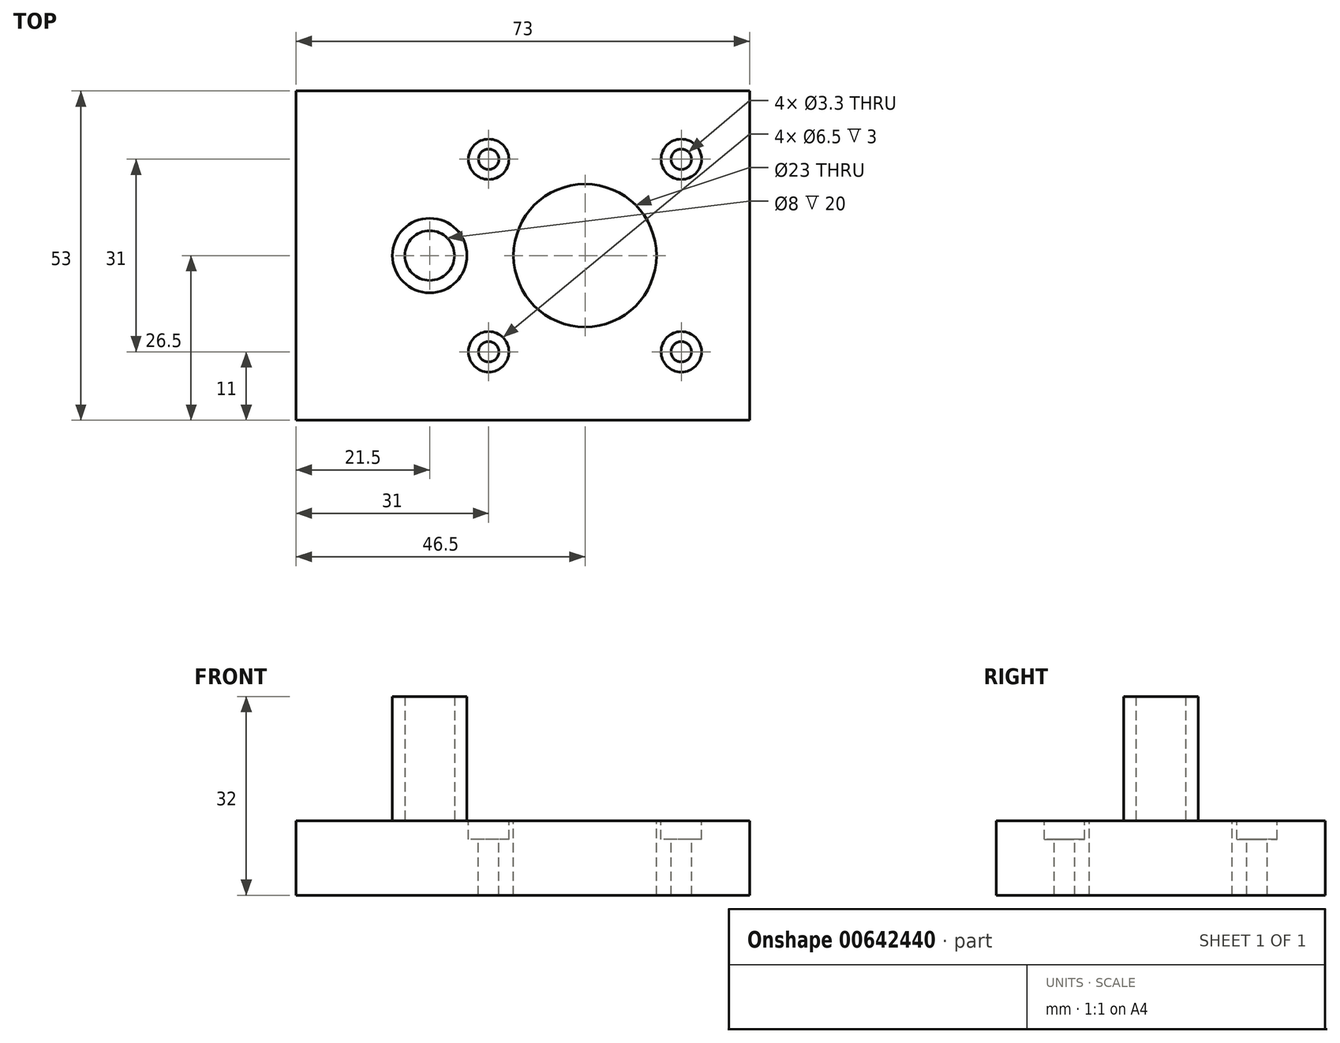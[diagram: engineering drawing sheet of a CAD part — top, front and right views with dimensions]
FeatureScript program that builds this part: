
annotation { "Feature Type Name" : "Feature", "Feature Type Description" : "" }
export const myFeature = defineFeature(function(context is Context, id is Id, definition is map)
    precondition{}
    {
        {
            var Q0;
            Q0=qCreatedBy(makeId("Top.planeOp"),FACE);
            var sketch = newSketch(context, id + "F0", { "sketchPlane" : qUnion([Q0])});
            skLineSegment(sketch, "E0.bottom", {"start": v(36.5, -26.5) * mm, "end": v(-36.5, -26.5) * mm});
            skLineSegment(sketch, "E0.top", {"start": v(36.5, 26.5) * mm, "end": v(-36.5, 26.5) * mm});
            skLineSegment(sketch, "E0.left", {"start": v(36.5, -26.5) * mm, "end": v(36.5, 26.5) * mm});
            skLineSegment(sketch, "E0.right", {"start": v(-36.5, -26.5) * mm, "end": v(-36.5, 26.5) * mm});
            skPoint(sketch, "E0.middle", {"position": v(0, 0) * mm});
            skLineSegment(sketch, "E1.bottom", {"start": v(25.5, -15.5) * mm, "end": v(-5.5, -15.5) * mm, "construction": true});
            skLineSegment(sketch, "E1.top", {"start": v(25.5, 15.5) * mm, "end": v(-5.5, 15.5) * mm, "construction": true});
            skLineSegment(sketch, "E1.left", {"start": v(25.5, -15.5) * mm, "end": v(25.5, 15.5) * mm, "construction": true});
            skLineSegment(sketch, "E1.right", {"start": v(-5.5, -15.5) * mm, "end": v(-5.5, 15.5) * mm, "construction": true});
            skPoint(sketch, "E1.middle", {"position": v(10, 0) * mm});
            skCircle(sketch, "E2", {"center": v(-15, 0) * mm, "radius": 6 * mm});
            skPoint(sketch, "E3", {"position": v(-5.5, 15.5) * mm});
            skPoint(sketch, "E4", {"position": v(25.5, 15.5) * mm});
            skPoint(sketch, "E5", {"position": v(25.5, -15.5) * mm});
            skPoint(sketch, "E6", {"position": v(-5.5, -15.5) * mm});
            skCircle(sketch, "E7", {"center": v(-15, 0) * mm, "radius": 4 * mm});
            skCircle(sketch, "E8", {"center": v(10, 0) * mm, "radius": 11.5 * mm});
            skSolve(sketch);
        }
        {
            var Q0;
            Q0 = qSketchRegion(id + "F0", true);
            var Q1;
            Q1=makeQuery(id+"F0.imprint","IMPRINT",FACE,{"disambiguationData":[TD([[makeQuery(id+"F0.imprint","IMPRINT",EDGE,{"derivedFrom":sQuery(id+"F0.wireOp",EDGE,"E2")}),1.0]])]});
            var Q2;
            Q2=makeQuery(id+"F0.imprint","IMPRINT",FACE,{"disambiguationData":[TD([[makeQuery(id+"F0.imprint","IMPRINT",EDGE,{"derivedFrom":sQuery(id+"F0.wireOp",EDGE,"E7")}),1.0]])]});
            extrude(context, id + "F1", {"entities" : qUnion([Q0, Q1, Q2]), "oppositeDirection" : true, "depth" : 12 * mm, "offsetDistance" : 25 * mm});
        }
        {
            var Q0;
            Q0=makeQuery(id+"F0.imprint","IMPRINT",FACE,{"disambiguationData":[TD([[makeQuery(id+"F0.imprint","IMPRINT",EDGE,{"derivedFrom":sQuery(id+"F0.wireOp",EDGE,"E2")}),1.0]])]});
            extrude(context, id + "F2", {"entities" : qUnion([Q0]), "operationType" : NewBodyOperationType.ADD, "depth" : 20 * mm, "offsetDistance" : 25 * mm});
        }
        {
            var Q0;
            Q0=sQuery(id+"F0.wireOp",VERTEX,"E3");
            var Q1;
            Q1=sQuery(id+"F0.wireOp",VERTEX,"E4");
            var Q2;
            Q2=sQuery(id+"F0.wireOp",VERTEX,"E5");
            var Q3;
            Q3=sQuery(id+"F0.wireOp",VERTEX,"E6");
            var Q4;
            Q4=makeQuery(id+"F1.opExtrude","SWEPT_BODY",BODY,{"disambiguationData":[OSD([sQuery(id+"F0.wireOp",EDGE,"E0.bottom"),sQuery(id+"F0.wireOp",EDGE,"E0.top"),sQuery(id+"F0.wireOp",EDGE,"E0.left"),sQuery(id+"F0.wireOp",EDGE,"E0.right"),sQuery(id+"F0.wireOp",EDGE,"E8")])]});
            hole(context, id + "F3", {"style" : HoleStyle.C_BORE, "endStyle" : HoleEndStyle.THROUGH, "standardTappedOrClearance" : lookupTablePath({ "standard" : "ISO", "fit" : "Normal", "size" : "M3", "type" : "Clearance" }), "standardBlindInLast" : lookupTablePath({ "fit" : "Standard", "standard" : "ISO", "size" : "M3", "type" : "Clearance" }), "holeDiameter" : 3.3 * mm, "cBoreDiameter" : 6.5 * mm, "cBoreDepth" : 3 * mm, "majorDiameter" : 5 * mm, "isTappedThrough" : true, "tappedDepth" : 12 * mm, "tapClearance" : 3, "locations" : qUnion([Q0, Q1, Q2, Q3]), "scope" : qUnion([Q4])});
        }
    });
